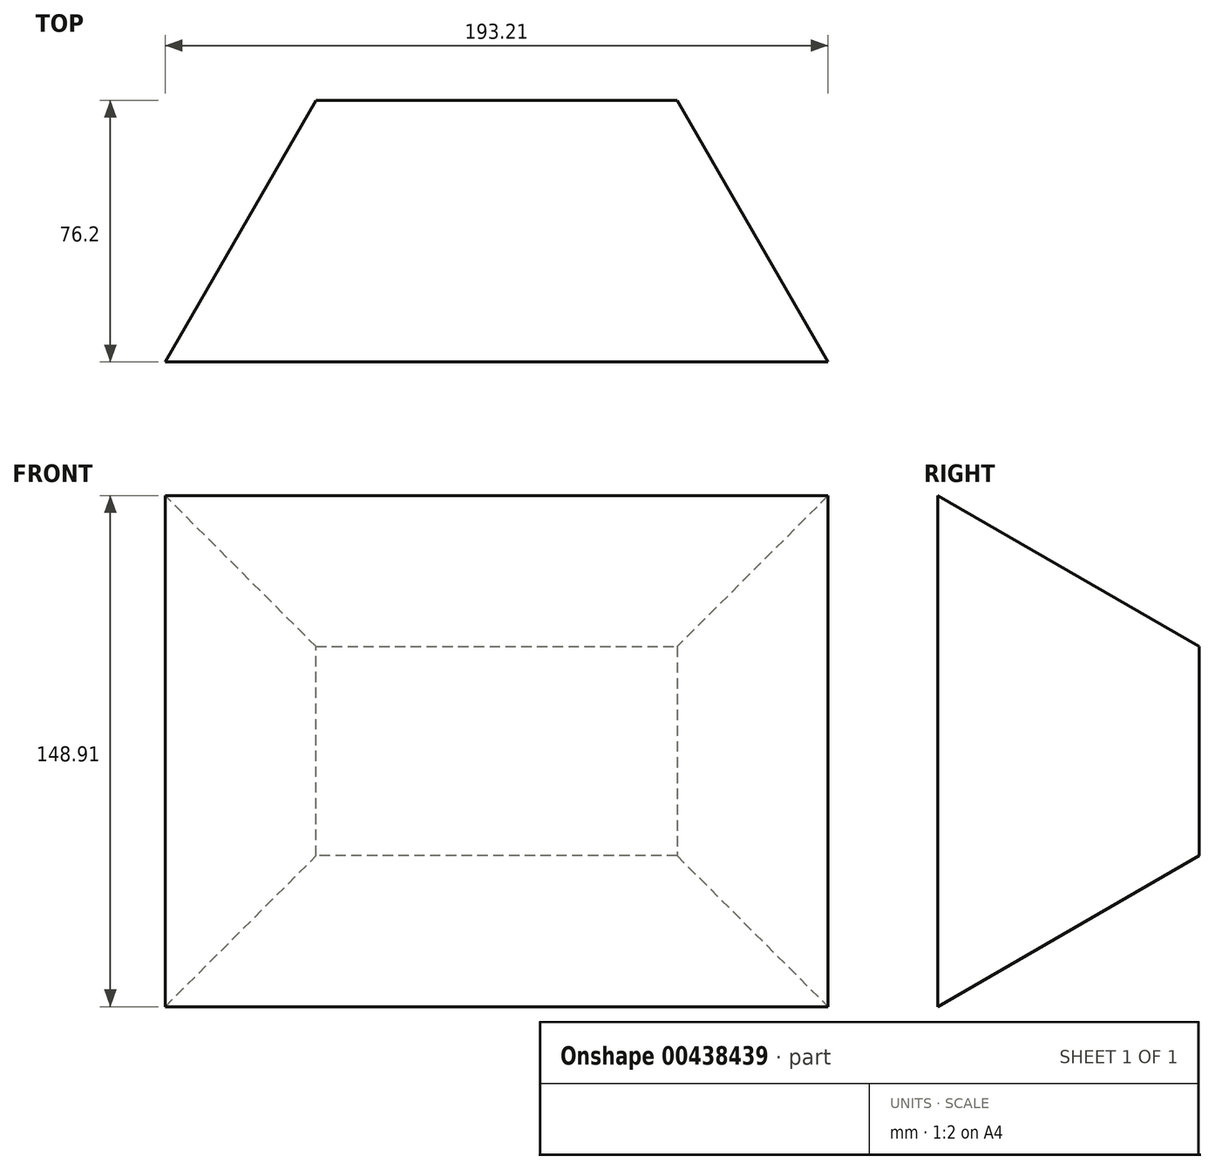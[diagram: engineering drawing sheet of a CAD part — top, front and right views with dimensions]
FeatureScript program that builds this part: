
annotation { "Feature Type Name" : "Feature", "Feature Type Description" : "" }
export const myFeature = defineFeature(function(context is Context, id is Id, definition is map)
    precondition{}
    {
        {
            var Q0;
            Q0=qCreatedBy(makeId("Front.planeOp"),FACE);
            var sketch = newSketch(context, id + "F0", { "sketchPlane" : qUnion([Q0])});
            skLineSegment(sketch, "E0.bottom", {"start": v(0, 0) * mm, "end": v(105.23, 0) * mm});
            skLineSegment(sketch, "E0.top", {"start": v(0, -60.93) * mm, "end": v(105.23, -60.93) * mm});
            skLineSegment(sketch, "E0.left", {"start": v(0, 0) * mm, "end": v(0, -60.93) * mm});
            skLineSegment(sketch, "E0.right", {"start": v(105.23, 0) * mm, "end": v(105.23, -60.93) * mm});
            skSolve(sketch);
        }
        {
            var Q0;
            Q0=makeQuery(id+"F0.imprint","IMPRINT",FACE,{"disambiguationData":[TD([[makeQuery(id+"F0.imprint","IMPRINT",EDGE,{"derivedFrom":sQuery(id+"F0.wireOp",EDGE,"E0.bottom")}),-1.0]])]});
            extrude(context, id + "F1", {"entities" : qUnion([Q0]), "depth" : 76.2 * mm, "hasDraft" : true, "draftAngle" : 30 * degree});
        }
    });
